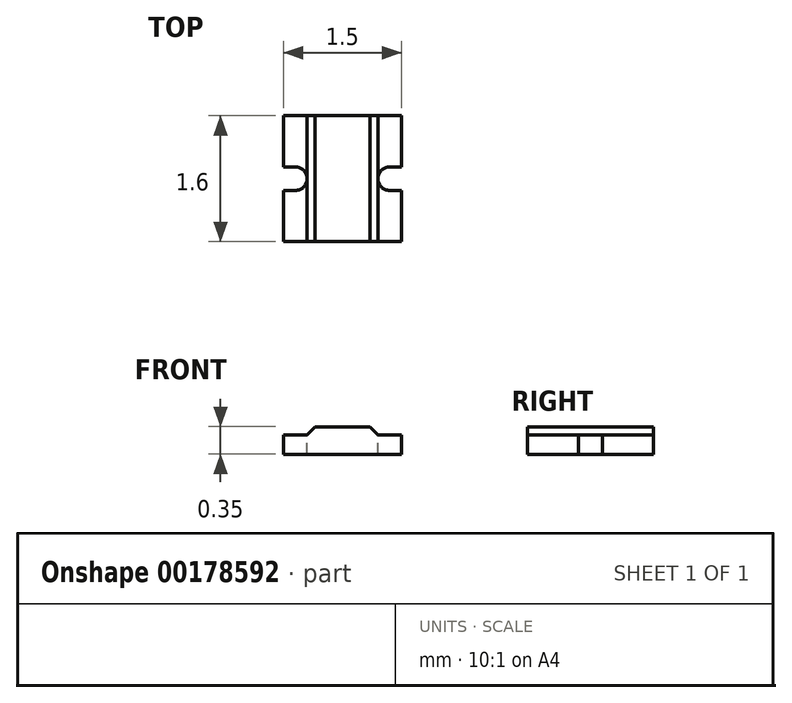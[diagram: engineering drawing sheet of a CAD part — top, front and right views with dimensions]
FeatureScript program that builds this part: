
annotation { "Feature Type Name" : "Feature", "Feature Type Description" : "" }
export const myFeature = defineFeature(function(context is Context, id is Id, definition is map)
    precondition{}
    {
        {
            var Q0;
            Q0=qCreatedBy(makeId("Front.planeOp"),FACE);
            var sketch = newSketch(context, id + "F0", { "sketchPlane" : qUnion([Q0])});
            skLineSegment(sketch, "E0.bottom", {"start": v(0.75, 0.13) * mm, "end": v(0.45, 0.13) * mm});
            skLineSegment(sketch, "E0.top", {"start": v(0.75, -0.13) * mm, "end": v(-0.75, -0.13) * mm});
            skLineSegment(sketch, "E0.left", {"start": v(0.75, 0.13) * mm, "end": v(0.75, -0.13) * mm});
            skLineSegment(sketch, "E0.right", {"start": v(-0.75, 0.13) * mm, "end": v(-0.75, -0.13) * mm});
            skPoint(sketch, "E0.middle", {"position": v(0, 0) * mm});
            skLineSegment(sketch, "E1.top", {"start": v(0.35, 0.22) * mm, "end": v(-0.35, 0.22) * mm});
            skLineSegment(sketch, "E2", {"start": v(0.35, 0.22) * mm, "end": v(0.45, 0.12) * mm});
            skLineSegment(sketch, "E3", {"start": v(-0.35, 0.22) * mm, "end": v(-0.45, 0.12) * mm});
            skLineSegment(sketch, "E4.trimOffspring", {"start": v(-0.45, 0.13) * mm, "end": v(-0.75, 0.13) * mm});
            skSolve(sketch);
        }
        {
            var Q0;
            Q0 = qSketchRegion(id + "F0", true);
            extrude(context, id + "F1", {"entities" : qUnion([Q0]), "depth" : 1.6 * mm});
        }
        {
            var Q0;
            Q0=makeQuery(id+"F1.opExtrude","SWEPT_FACE",FACE,{"disambiguationData":[OSD([sQuery(id+"F0.wireOp",EDGE,"E4.trimOffspring")])]});
            var sketch = newSketch(context, id + "F2", { "sketchPlane" : qUnion([Q0])});
            skLineSegment(sketch, "E5.bottom", {"start": v(-0.75, -0.65) * mm, "end": v(-0.45, -0.65) * mm});
            skLineSegment(sketch, "E5.top", {"start": v(-0.75, -0.95) * mm, "end": v(-0.45, -0.95) * mm});
            skLineSegment(sketch, "E5.left", {"start": v(-0.75, -0.65) * mm, "end": v(-0.75, -0.95) * mm});
            skLineSegment(sketch, "E5.right", {"start": v(-0.45, -0.65) * mm, "end": v(-0.45, -0.95) * mm});
            skSolve(sketch);
        }
        {
            var Q0;
            Q0=makeQuery(id+"F2.imprint","IMPRINT",FACE,{"disambiguationData":[TD([[makeQuery(id+"F2.imprint","IMPRINT",EDGE,{"derivedFrom":sQuery(id+"F2.wireOp",EDGE,"E5.bottom")}),-1.0]])]});
            extrude(context, id + "F3", {"entities" : qUnion([Q0]), "operationType" : NewBodyOperationType.REMOVE, "oppositeDirection" : true, "depth" : 0.3 * mm});
        }
        {
            var Q0;
            Q0=makeQuery(id+"F1.opExtrude","SWEPT_FACE",FACE,{"disambiguationData":[OSD([sQuery(id+"F0.wireOp",EDGE,"E0.bottom")])]});
            var sketch = newSketch(context, id + "F4", { "sketchPlane" : qUnion([Q0])});
            skLineSegment(sketch, "E6.bottom", {"start": v(0.75, -0.65) * mm, "end": v(0.45, -0.65) * mm});
            skLineSegment(sketch, "E6.top", {"start": v(0.75, -0.95) * mm, "end": v(0.45, -0.95) * mm});
            skLineSegment(sketch, "E6.left", {"start": v(0.75, -0.65) * mm, "end": v(0.75, -0.95) * mm});
            skLineSegment(sketch, "E6.right", {"start": v(0.45, -0.65) * mm, "end": v(0.45, -0.95) * mm});
            skSolve(sketch);
        }
        {
            var Q0;
            Q0=makeQuery(id+"F4.imprint","IMPRINT",FACE,{"disambiguationData":[TD([[makeQuery(id+"F4.imprint","IMPRINT",EDGE,{"derivedFrom":sQuery(id+"F4.wireOp",EDGE,"E6.bottom")}),1.0]])]});
            extrude(context, id + "F5", {"entities" : qUnion([Q0]), "operationType" : NewBodyOperationType.REMOVE, "oppositeDirection" : true, "depth" : 0.3 * mm});
        }
        {
            var Q0;
            Q0=makeQuery(id+"F5.boolean.opBoolean","COPY",EDGE,{"derivedFrom":makeQuery(id+"F5.opExtrude","SWEPT_EDGE",EDGE,{"disambiguationData":[OSD([sQuery(id+"F0.wireOp",EDGE,"E0.bottom"),sQuery(id+"F0.wireOp",EDGE,"E2"),sQuery(id+"F4.wireOp",EDGE,"E6.bottom"),sQuery(id+"F4.wireOp",EDGE,"E6.right")])]})});
            var Q1;
            Q1=makeQuery(id+"F3.boolean.opBoolean","COPY",EDGE,{"derivedFrom":makeQuery(id+"F3.opExtrude","SWEPT_EDGE",EDGE,{"disambiguationData":[OSD([sQuery(id+"F0.wireOp",EDGE,"E3"),sQuery(id+"F0.wireOp",EDGE,"E4.trimOffspring"),sQuery(id+"F2.wireOp",EDGE,"E5.bottom"),sQuery(id+"F2.wireOp",EDGE,"E5.right")])]})});
            var Q2;
            Q2=makeQuery(id+"F3.boolean.opBoolean","COPY",EDGE,{"derivedFrom":makeQuery(id+"F3.opExtrude","SWEPT_EDGE",EDGE,{"disambiguationData":[OSD([sQuery(id+"F0.wireOp",EDGE,"E3"),sQuery(id+"F0.wireOp",EDGE,"E4.trimOffspring"),sQuery(id+"F2.wireOp",EDGE,"E5.top"),sQuery(id+"F2.wireOp",EDGE,"E5.right")])]})});
            var Q3;
            Q3=makeQuery(id+"F5.boolean.opBoolean","COPY",EDGE,{"derivedFrom":makeQuery(id+"F5.opExtrude","SWEPT_EDGE",EDGE,{"disambiguationData":[OSD([sQuery(id+"F0.wireOp",EDGE,"E0.bottom"),sQuery(id+"F0.wireOp",EDGE,"E2"),sQuery(id+"F4.wireOp",EDGE,"E6.top"),sQuery(id+"F4.wireOp",EDGE,"E6.right")])]})});
            fillet(context, id + "F6", {"entities" : qUnion([Q0, Q1, Q2, Q3]), "radius" : 0.15 * mm, "tangentPropagation" : true, "allowEdgeOverflow" : false});
        }
    });
